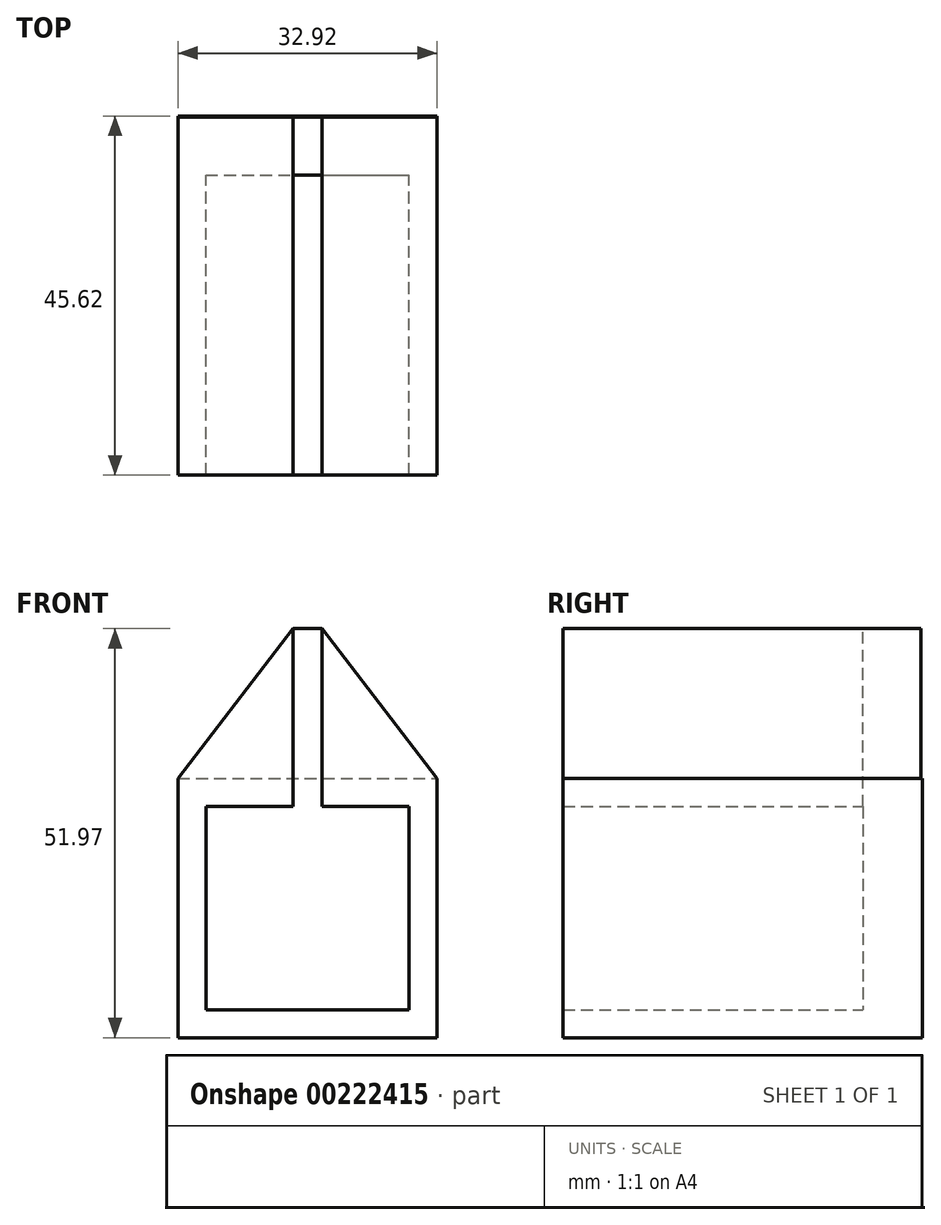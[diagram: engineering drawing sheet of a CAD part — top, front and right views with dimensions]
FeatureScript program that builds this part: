
annotation { "Feature Type Name" : "Feature", "Feature Type Description" : "" }
export const myFeature = defineFeature(function(context is Context, id is Id, definition is map)
    precondition{}
    {
        {
            var Q0;
            Q0=qCreatedBy(makeId("Top.planeOp"),FACE);
            var sketch = newSketch(context, id + "F0", { "sketchPlane" : qUnion([Q0])});
            skLineSegment(sketch, "E0.bottom", {"start": v(0, 0) * mm, "end": v(32.92, 0) * mm});
            skLineSegment(sketch, "E0.top", {"start": v(0, -32.92) * mm, "end": v(32.92, -32.92) * mm});
            skLineSegment(sketch, "E0.left", {"start": v(0, 0) * mm, "end": v(0, -32.92) * mm});
            skLineSegment(sketch, "E0.right", {"start": v(32.92, 0) * mm, "end": v(32.92, -32.92) * mm});
            skSolve(sketch);
        }
        {
            var Q0;
            Q0 = qSketchRegion(id + "F0", true);
            extrude(context, id + "F1", {"entities" : qUnion([Q0]), "depth" : 32.92 * mm});
        }
        {
            var Q0;
            Q0=makeQuery(id+"F1.opExtrude","SWEPT_FACE",FACE,{"disambiguationData":[OSD([sQuery(id+"F0.wireOp",EDGE,"E0.top")])]});
            var sketch = newSketch(context, id + "F2", { "sketchPlane" : qUnion([Q0])});
            skLineSegment(sketch, "E1.bottom", {"start": v(0, 32.92) * mm, "end": v(32.92, 32.92) * mm});
            skLineSegment(sketch, "E1.top", {"start": v(0, 0) * mm, "end": v(32.92, 0) * mm});
            skLineSegment(sketch, "E1.left", {"start": v(0, 32.92) * mm, "end": v(0, 0) * mm});
            skLineSegment(sketch, "E1.right", {"start": v(32.92, 32.92) * mm, "end": v(32.92, 0) * mm});
            skLineSegment(sketch, "E2.bottom", {"start": v(3.56, 29.36) * mm, "end": v(29.36, 29.36) * mm});
            skLineSegment(sketch, "E2.top", {"start": v(3.56, 3.56) * mm, "end": v(29.36, 3.56) * mm});
            skLineSegment(sketch, "E2.left", {"start": v(3.56, 29.36) * mm, "end": v(3.56, 3.56) * mm});
            skLineSegment(sketch, "E2.right", {"start": v(29.36, 29.36) * mm, "end": v(29.36, 3.56) * mm});
            skLineSegment(sketch, "E3.bottom", {"start": v(8, 27.56) * mm, "end": v(27.56, 27.56) * mm});
            skLineSegment(sketch, "E3.top", {"start": v(8, 8) * mm, "end": v(27.56, 8) * mm});
            skLineSegment(sketch, "E3.left", {"start": v(8, 27.56) * mm, "end": v(8, 8) * mm});
            skLineSegment(sketch, "E3.right", {"start": v(27.56, 27.56) * mm, "end": v(27.56, 8) * mm});
            skSolve(sketch);
        }
        {
            var Q0;
            Q0=makeQuery(id+"F2.imprint","IMPRINT",FACE,{"disambiguationData":[TD([[makeQuery(id+"F2.imprint","IMPRINT",EDGE,{"derivedFrom":sQuery(id+"F2.wireOp",EDGE,"E1.bottom")}),-1.0]])]});
            extrude(context, id + "F3", {"entities" : qUnion([Q0]), "operationType" : NewBodyOperationType.ADD, "depth" : 76.2 * mm});
        }
        {
            var Q0;
            Q0=makeQuery(id+"F3.boolean.opBoolean","MERGE",FACE,{"derivedFrom":[makeQuery(id+"F1.opExtrude","CAP_FACE",FACE,{"disambiguationData":[OSD([sQuery(id+"F0.wireOp",EDGE,"E0.bottom"),sQuery(id+"F0.wireOp",EDGE,"E0.top"),sQuery(id+"F0.wireOp",EDGE,"E0.left"),sQuery(id+"F0.wireOp",EDGE,"E0.right")])],"isStart":false}),makeQuery(id+"F3.opExtrude","SWEPT_FACE",FACE,{"disambiguationData":[OSD([sQuery(id+"F2.wireOp",EDGE,"E1.bottom")])]})]});
            var sketch = newSketch(context, id + "F4", { "sketchPlane" : qUnion([Q0])});
            skLineSegment(sketch, "E4.bottom", {"start": v(14.6, -109.12) * mm, "end": v(18.31, -109.12) * mm});
            skLineSegment(sketch, "E4.top", {"start": v(14.6, -32.92) * mm, "end": v(18.31, -32.92) * mm});
            skLineSegment(sketch, "E4.left", {"start": v(14.6, -109.12) * mm, "end": v(14.6, -32.92) * mm});
            skLineSegment(sketch, "E4.right", {"start": v(18.31, -109.12) * mm, "end": v(18.31, -32.92) * mm});
            skSolve(sketch);
        }
        {
            var Q0;
            Q0=makeQuery(id+"F4.imprint","IMPRINT",FACE,{"disambiguationData":[TD([[makeQuery(id+"F4.imprint","IMPRINT",EDGE,{"derivedFrom":sQuery(id+"F4.wireOp",EDGE,"E4.bottom")}),1.0]])]});
            extrude(context, id + "F5", {"entities" : qUnion([Q0]), "operationType" : NewBodyOperationType.REMOVE, "oppositeDirection" : true, "depth" : 5.08 * mm});
        }
        {
            var Q0;
            Q0=makeQuery(id+"F3.opExtrude","CAP_FACE",FACE,{"disambiguationData":[OSD([sQuery(id+"F2.wireOp",EDGE,"E1.bottom"),sQuery(id+"F2.wireOp",EDGE,"E1.top"),sQuery(id+"F2.wireOp",EDGE,"E1.left"),sQuery(id+"F2.wireOp",EDGE,"E1.right"),sQuery(id+"F2.wireOp",EDGE,"E2.bottom"),sQuery(id+"F2.wireOp",EDGE,"E2.top"),sQuery(id+"F2.wireOp",EDGE,"E2.left"),sQuery(id+"F2.wireOp",EDGE,"E2.right")])],"isStart":false});
            var sketch = newSketch(context, id + "F6", { "sketchPlane" : qUnion([Q0])});
            skLineSegment(sketch, "E5", {"start": v(14.6, 32.92) * mm, "end": v(14.6, 51.97) * mm});
            skLineSegment(sketch, "E6", {"start": v(14.6, 51.97) * mm, "end": v(0, 32.92) * mm});
            skLineSegment(sketch, "E7", {"start": v(0, 32.92) * mm, "end": v(14.6, 32.92) * mm});
            skLineSegment(sketch, "E8", {"start": v(18.31, 32.92) * mm, "end": v(18.31, 51.97) * mm});
            skLineSegment(sketch, "E9", {"start": v(18.31, 51.97) * mm, "end": v(32.92, 32.92) * mm});
            skLineSegment(sketch, "E10", {"start": v(32.92, 32.92) * mm, "end": v(18.31, 32.92) * mm});
            skSolve(sketch);
        }
        {
            var Q0;
            Q0=makeQuery(id+"F6.imprint","IMPRINT",FACE,{"disambiguationData":[TD([[makeQuery(id+"F6.imprint","IMPRINT",EDGE,{"derivedFrom":sQuery(id+"F6.wireOp",EDGE,"E5")}),1.0]])]});
            var Q1;
            Q1=makeQuery(id+"F6.imprint","IMPRINT",FACE,{"disambiguationData":[TD([[makeQuery(id+"F6.imprint","IMPRINT",EDGE,{"derivedFrom":sQuery(id+"F6.wireOp",EDGE,"E8")}),-1.0]])]});
            extrude(context, id + "F7", {"entities" : qUnion([Q0, Q1]), "operationType" : NewBodyOperationType.ADD, "oppositeDirection" : true, "depth" : 76.2 * mm});
        }
        {
            var Q0;
            Q0=makeQuery(id+"F2.imprint","IMPRINT",FACE,{"disambiguationData":[TD([[makeQuery(id+"F2.imprint","IMPRINT",EDGE,{"derivedFrom":sQuery(id+"F2.wireOp",EDGE,"E1.bottom")}),-1.0]])]});
            var sketch = newSketch(context, id + "F8", { "sketchPlane" : qUnion([Q0])});
            skLineSegment(sketch, "E11", {"start": v(14.6, 32.92) * mm, "end": v(14.6, 51.97) * mm});
            skLineSegment(sketch, "E12", {"start": v(14.6, 51.97) * mm, "end": v(18.31, 51.97) * mm});
            skLineSegment(sketch, "E13", {"start": v(18.31, 51.97) * mm, "end": v(18.31, 32.92) * mm});
            skLineSegment(sketch, "E14", {"start": v(18.31, 32.92) * mm, "end": v(14.6, 32.92) * mm});
            skLineSegment(sketch, "E15", {"start": v(14.6, 51.97) * mm, "end": v(0, 32.92) * mm});
            skLineSegment(sketch, "E16", {"start": v(0, 32.92) * mm, "end": v(14.6, 32.92) * mm});
            skLineSegment(sketch, "E17", {"start": v(18.31, 51.97) * mm, "end": v(32.92, 32.92) * mm});
            skLineSegment(sketch, "E18", {"start": v(32.92, 32.92) * mm, "end": v(18.31, 32.92) * mm});
            skSolve(sketch);
        }
        {
            var Q0;
            Q0=makeQuery(id+"F8.imprint","IMPRINT",FACE,{"disambiguationData":[TD([[makeQuery(id+"F8.imprint","IMPRINT",EDGE,{"derivedFrom":sQuery(id+"F8.wireOp",EDGE,"E13")}),1.0]])]});
            var Q1;
            Q1=makeQuery(id+"F8.imprint","IMPRINT",FACE,{"disambiguationData":[TD([[makeQuery(id+"F8.imprint","IMPRINT",EDGE,{"derivedFrom":sQuery(id+"F8.wireOp",EDGE,"E11")}),-1.0]])]});
            var Q2;
            Q2=makeQuery(id+"F8.imprint","IMPRINT",FACE,{"disambiguationData":[TD([[makeQuery(id+"F8.imprint","IMPRINT",EDGE,{"derivedFrom":sQuery(id+"F8.wireOp",EDGE,"E11")}),1.0]])]});
            extrude(context, id + "F9", {"entities" : qUnion([Q0, Q1, Q2]), "operationType" : NewBodyOperationType.ADD, "oppositeDirection" : true, "depth" : 7.34 * mm});
        }
        {
            var Q0;
            Q0=makeQuery(id+"F1.opExtrude","SWEPT_FACE",FACE,{"disambiguationData":[OSD([sQuery(id+"F0.wireOp",EDGE,"E0.bottom")])]});
            extrude(context, id + "F10", {"entities" : qUnion([Q0]), "operationType" : NewBodyOperationType.REMOVE, "oppositeDirection" : true, "depth" : 25.4 * mm});
        }
        {
            var Q0;
            Q0=makeQuery(id+"F7.boolean.opBoolean","MERGE",FACE,{"derivedFrom":[makeQuery(id+"F3.opExtrude","CAP_FACE",FACE,{"disambiguationData":[OSD([sQuery(id+"F2.wireOp",EDGE,"E1.bottom"),sQuery(id+"F2.wireOp",EDGE,"E1.top"),sQuery(id+"F2.wireOp",EDGE,"E1.left"),sQuery(id+"F2.wireOp",EDGE,"E1.right"),sQuery(id+"F2.wireOp",EDGE,"E2.bottom"),sQuery(id+"F2.wireOp",EDGE,"E2.top"),sQuery(id+"F2.wireOp",EDGE,"E2.left"),sQuery(id+"F2.wireOp",EDGE,"E2.right")])],"isStart":false}),makeQuery(id+"F7.opExtrude","CAP_FACE",FACE,{"disambiguationData":[OSD([sQuery(id+"F6.wireOp",EDGE,"E5"),sQuery(id+"F6.wireOp",EDGE,"E6"),sQuery(id+"F6.wireOp",EDGE,"E7")])],"isStart":true}),makeQuery(id+"F7.opExtrude","CAP_FACE",FACE,{"disambiguationData":[OSD([sQuery(id+"F6.wireOp",EDGE,"E8"),sQuery(id+"F6.wireOp",EDGE,"E9"),sQuery(id+"F6.wireOp",EDGE,"E10")])],"isStart":true})]});
            extrude(context, id + "F11", {"entities" : qUnion([Q0]), "operationType" : NewBodyOperationType.REMOVE, "oppositeDirection" : true, "depth" : 38.1 * mm});
        }
    });
